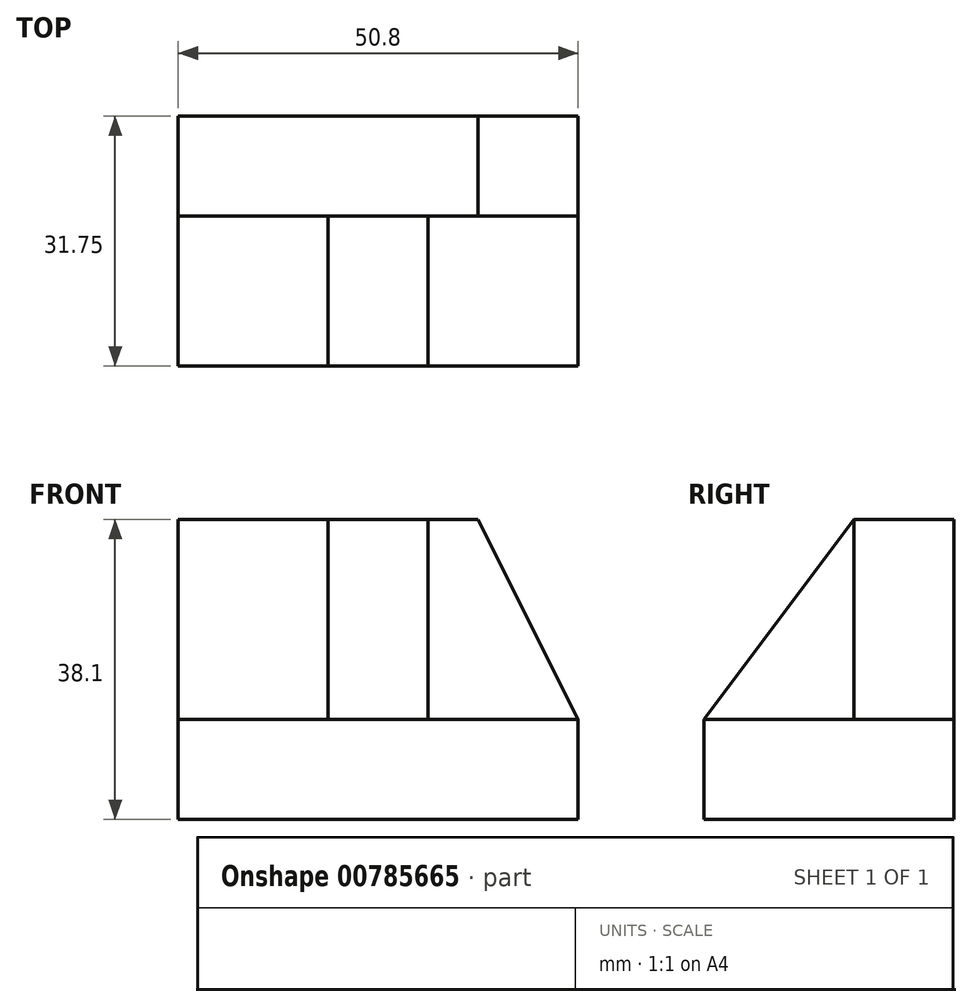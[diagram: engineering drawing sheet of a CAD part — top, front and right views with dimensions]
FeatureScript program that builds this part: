
annotation { "Feature Type Name" : "Feature", "Feature Type Description" : "" }
export const myFeature = defineFeature(function(context is Context, id is Id, definition is map)
    precondition{}
    {
        {
            var Q0;
            Q0=qCreatedBy(makeId("Front.planeOp"),FACE);
            var sketch = newSketch(context, id + "F0", { "sketchPlane" : qUnion([Q0])});
            skLineSegment(sketch, "E0", {"start": v(0, 0) * mm, "end": v(50.8, 0) * mm});
            skLineSegment(sketch, "E1", {"start": v(50.8, 0) * mm, "end": v(50.8, 38.1) * mm});
            skLineSegment(sketch, "E2", {"start": v(50.8, 38.1) * mm, "end": v(0, 38.1) * mm});
            skLineSegment(sketch, "E3", {"start": v(0, 38.1) * mm, "end": v(0, 0) * mm});
            skSolve(sketch);
        }
        {
            var Q0;
            Q0 = qSketchRegion(id + "F0", true);
            extrude(context, id + "F1", {"entities" : qUnion([Q0]), "depth" : 31.75 * mm, "offsetDistance" : 25.4 * mm});
        }
        {
            var Q0;
            Q0=makeQuery(id+"F1.opExtrude","CAP_FACE",FACE,{"disambiguationData":[OSD([sQuery(id+"F0.wireOp",EDGE,"E0"),sQuery(id+"F0.wireOp",EDGE,"E1"),sQuery(id+"F0.wireOp",EDGE,"E2"),sQuery(id+"F0.wireOp",EDGE,"E3")])],"isStart":false});
            var sketch = newSketch(context, id + "F2", { "sketchPlane" : qUnion([Q0])});
            skLineSegment(sketch, "E4", {"start": v(0, 0) * mm, "end": v(0, 12.7) * mm});
            skLineSegment(sketch, "E5", {"start": v(0, 12.7) * mm, "end": v(19.05, 12.7) * mm});
            skLineSegment(sketch, "E6", {"start": v(19.05, 12.7) * mm, "end": v(19.05, 38.1) * mm});
            skSolve(sketch);
        }
        {
            var Q0;
            Q0 = qSketchRegion(id + "F2", true);
            var Q1;
            {var subQ0=sQuery(id+"F2.wireOp",EDGE,"E5");Q1=makeQuery(id+"F2.imprint","IMPRINT",FACE,{"disambiguationData":[TD([[makeQuery(id+"F2.imprint","IMPRINT",EDGE,{"derivedFrom":subQ0}),1.0]])]});}
            extrude(context, id + "F3", {"entities" : qUnion([Q0, Q1]), "operationType" : NewBodyOperationType.REMOVE, "oppositeDirection" : true, "depth" : 19.05 * mm, "offsetDistance" : 25.4 * mm});
        }
        {
            var Q0;
            Q0=makeQuery(id+"F1.opExtrude","CAP_FACE",FACE,{"disambiguationData":[OSD([sQuery(id+"F0.wireOp",EDGE,"E0"),sQuery(id+"F0.wireOp",EDGE,"E1"),sQuery(id+"F0.wireOp",EDGE,"E2"),sQuery(id+"F0.wireOp",EDGE,"E3")])],"isStart":false});
            var sketch = newSketch(context, id + "F4", { "sketchPlane" : qUnion([Q0])});
            skLineSegment(sketch, "E7", {"start": v(50.8, 0) * mm, "end": v(50.8, 12.7) * mm});
            skLineSegment(sketch, "E8", {"start": v(50.8, 12.7) * mm, "end": v(31.75, 12.7) * mm});
            skLineSegment(sketch, "E9", {"start": v(31.75, 12.7) * mm, "end": v(31.75, 38.1) * mm});
            skLineSegment(sketch, "E10", {"start": v(31.75, 38.1) * mm, "end": v(50.8, 38.1) * mm});
            skLineSegment(sketch, "E11", {"start": v(50.8, 38.1) * mm, "end": v(50.8, 12.7) * mm});
            skSolve(sketch);
        }
        {
            var Q0;
            Q0=makeQuery(id+"F4.imprint","IMPRINT",FACE,{"disambiguationData":[TD([[makeQuery(id+"F4.imprint","IMPRINT",EDGE,{"derivedFrom":sQuery(id+"F4.wireOp",EDGE,"E8")}),-1.0]])]});
            extrude(context, id + "F5", {"entities" : qUnion([Q0]), "operationType" : NewBodyOperationType.REMOVE, "oppositeDirection" : true, "depth" : 19.05 * mm, "offsetDistance" : 25.4 * mm});
        }
        {
            var Q0;
            Q0=makeQuery(id+"F5.boolean.opBoolean","COPY",FACE,{"derivedFrom":makeQuery(id+"F5.opExtrude","SWEPT_FACE",FACE,{"disambiguationData":[OSD([sQuery(id+"F4.wireOp",EDGE,"E9")])]})});
            var sketch = newSketch(context, id + "F6", { "sketchPlane" : qUnion([Q0])});
            skLineSegment(sketch, "E12", {"start": v(-31.75, 12.7) * mm, "end": v(-12.7, 38.1) * mm});
            skSolve(sketch);
        }
        {
            var Q0;
            Q0=makeQuery(id+"F6.imprint","IMPRINT",FACE,{"disambiguationData":[TD([[makeQuery(id+"F6.imprint","IMPRINT",EDGE,{"derivedFrom":sQuery(id+"F6.wireOp",EDGE,"E12")}),1.0]])]});
            extrude(context, id + "F7", {"entities" : qUnion([Q0]), "operationType" : NewBodyOperationType.REMOVE, "oppositeDirection" : true, "depth" : 25.4 * mm, "offsetDistance" : 25.4 * mm});
        }
        {
            var Q0;
            Q0=makeQuery(id+"F5.boolean.opBoolean","COPY",FACE,{"derivedFrom":makeQuery(id+"F5.opExtrude","CAP_FACE",FACE,{"disambiguationData":[OSD([sQuery(id+"F4.wireOp",EDGE,"E8"),sQuery(id+"F4.wireOp",EDGE,"E9"),sQuery(id+"F4.wireOp",EDGE,"E10"),sQuery(id+"F4.wireOp",EDGE,"E11")])],"isStart":false})});
            var sketch = newSketch(context, id + "F8", { "sketchPlane" : qUnion([Q0])});
            skLineSegment(sketch, "E13", {"start": v(31.75, 38.1) * mm, "end": v(38.1, 38.1) * mm});
            skLineSegment(sketch, "E14", {"start": v(38.1, 38.1) * mm, "end": v(50.8, 12.7) * mm});
            skSolve(sketch);
        }
        {
            var Q0;
            {var subQ0=sQuery(id+"F8.wireOp",EDGE,"E14");Q0=makeQuery(id+"F8.imprint","IMPRINT",FACE,{"disambiguationData":[TD([[makeQuery(id+"F8.imprint","IMPRINT",EDGE,{"derivedFrom":subQ0}),1.0]])]});}
            extrude(context, id + "F9", {"entities" : qUnion([Q0]), "operationType" : NewBodyOperationType.REMOVE, "oppositeDirection" : true, "depth" : 25.4 * mm, "offsetDistance" : 25.4 * mm});
        }
    });
